FCSTD DOCUMENT  (FreeCAD 0.18RUnknown)
Label: vga_usb_serial_cutout
License: Public Domain
LicenseURL: http://en.wikipedia.org/wiki/Public_domain
objects: Sketcher::SketchObject×1, TechDraw::DrawSVGTemplate×1, TechDraw::DrawViewPart×1, TechDraw::DrawPage×1
note: 1 computed .brp shape members not serialized (recipe doc carries the construction recipe); baked Part::Feature solids carry a one-line shape summary decoded from their .brp

FEATURE [Sketcher::SketchObject] Sketch
  sketch-geometry (56):
    g0: LineSegment [constr] StartX=-35 StartY=1.6 StartZ=0 EndX=-0.6 EndY=1.6 EndZ=0
    g1: LineSegment [constr] StartX=35 StartY=1.6 StartZ=0 EndX=35 EndY=0 EndZ=0
    g2: LineSegment [constr] StartX=35 StartY=0 StartZ=0 EndX=-35 EndY=0 EndZ=0
    g3: LineSegment [constr] StartX=-35 StartY=0 StartZ=0 EndX=-35 EndY=1.6 EndZ=0
    g4: LineSegment [constr] StartX=-18.5 StartY=13.765 StartZ=0 EndX=-18.5 EndY=2.365 EndZ=0
    g5: Circle CenterX=-6 CenterY=8.065 CenterZ=0 NormalX=0 NormalY=0 NormalZ=1 AngleXU=0 Radius=1.55
    g6: Circle CenterX=-31 CenterY=8.065 CenterZ=0 NormalX=0 NormalY=0 NormalZ=1 AngleXU=0 Radius=1.55
    g7: LineSegment StartX=-25.35 StartY=13.765 StartZ=0 EndX=-11.65 EndY=13.765 EndZ=0
    g8: LineSegment StartX=-24.5389 StartY=2.365 StartZ=0 EndX=-12.4611 EndY=2.365 EndZ=0
    g9: LineSegment StartX=-28.6983 StartY=9.7746 StartZ=0 EndX=-27.8872 EndY=5.1746 EndZ=0
    g10: LineSegment StartX=-8.30165 StartY=9.7746 StartZ=0 EndX=-9.11276 EndY=5.1746 EndZ=0
    g11: ArcOfCircle CenterX=-24.5389 CenterY=5.765 CenterZ=0 NormalX=0 NormalY=0 NormalZ=1 AngleXU=0 Radius=3.4 StartAngle=3.31613 EndAngle=4.71239
    g12: ArcOfCircle CenterX=-12.4611 CenterY=5.765 CenterZ=0 NormalX=0 NormalY=0 NormalZ=1 AngleXU=0 Radius=3.4 StartAngle=4.71239 EndAngle=6.10865
    g13: ArcOfCircle CenterX=-11.65 CenterY=10.365 CenterZ=0 NormalX=0 NormalY=0 NormalZ=1 AngleXU=0 Radius=3.4 StartAngle=6.10865 EndAngle=7.85398
    g14: ArcOfCircle CenterX=-25.35 CenterY=10.365 CenterZ=0 NormalX=0 NormalY=0 NormalZ=1 AngleXU=0 Radius=3.4 StartAngle=1.5708 EndAngle=3.31613
    g15: LineSegment [constr] StartX=-28.75 StartY=13.765 StartZ=0 EndX=-28.75 EndY=2.365 EndZ=0
    g16: LineSegment [constr] StartX=-8.25 StartY=13.765 StartZ=0 EndX=-8.25 EndY=2.365 EndZ=0
    g17: GeomPoint X=-18.5 Y=8.065 Z=0
    g18: LineSegment StartX=-0.6 StartY=1.375 StartZ=0 EndX=-0.6 EndY=4.275 EndZ=0
    g19: LineSegment StartX=8.4 StartY=1.375 StartZ=0 EndX=8.4 EndY=4.275 EndZ=0
    g20: LineSegment StartX=-0.1 StartY=4.775 StartZ=0 EndX=7.9 EndY=4.775 EndZ=0
    g21: LineSegment StartX=7.9 StartY=0.875 StartZ=0 EndX=-0.1 EndY=0.875 EndZ=0
    g22: ArcOfCircle CenterX=-0.1 CenterY=4.275 CenterZ=0 NormalX=0 NormalY=0 NormalZ=1 AngleXU=0 Radius=0.5 StartAngle=1.5708 EndAngle=3.14159
    g23: ArcOfCircle CenterX=7.9 CenterY=4.275 CenterZ=0 NormalX=0 NormalY=0 NormalZ=1 AngleXU=0 Radius=0.5 StartAngle=0 EndAngle=1.5708
    g24: ArcOfCircle CenterX=7.9 CenterY=1.375 CenterZ=0 NormalX=0 NormalY=0 NormalZ=1 AngleXU=0 Radius=0.5 StartAngle=4.71239 EndAngle=6.28319
    g25: ArcOfCircle CenterX=-0.1 CenterY=1.375 CenterZ=0 NormalX=0 NormalY=0 NormalZ=1 AngleXU=0 Radius=0.5 StartAngle=3.14159 EndAngle=4.71239
    g26: LineSegment [constr] StartX=3.9 StartY=0.875 StartZ=0 EndX=3.9 EndY=1.375 EndZ=0
    g27: LineSegment [constr] StartX=8.4 StartY=1.6 StartZ=0 EndX=10.12 EndY=1.6 EndZ=0
    g28: LineSegment [constr] StartX=-0.6 StartY=2.825 StartZ=0 EndX=-0.1 EndY=2.825 EndZ=0
    g29: LineSegment [constr] StartX=0.4 StartY=4.275 StartZ=0 EndX=7.4 EndY=4.275 EndZ=0
    g30: LineSegment [constr] StartX=7.9 StartY=3.775 StartZ=0 EndX=7.9 EndY=1.875 EndZ=0
    g31: LineSegment [constr] StartX=7.4 StartY=1.375 StartZ=0 EndX=0.4 EndY=1.375 EndZ=0
    g32: LineSegment [constr] StartX=-0.1 StartY=1.875 StartZ=0 EndX=-0.1 EndY=3.775 EndZ=0
    g33: ArcOfCircle [constr] CenterX=7.4 CenterY=3.775 CenterZ=0 NormalX=0 NormalY=0 NormalZ=1 AngleXU=0 Radius=0.5 StartAngle=0 EndAngle=1.5708
    g34: ArcOfCircle [constr] CenterX=7.4 CenterY=1.875 CenterZ=0 NormalX=0 NormalY=0 NormalZ=1 AngleXU=0 Radius=0.5 StartAngle=4.71239 EndAngle=6.28319
    g35: ArcOfCircle [constr] CenterX=0.4 CenterY=1.875 CenterZ=0 NormalX=0 NormalY=0 NormalZ=1 AngleXU=0 Radius=0.5 StartAngle=3.14159 EndAngle=4.71239
    g36: ArcOfCircle [constr] CenterX=0.4 CenterY=3.775 CenterZ=0 NormalX=0 NormalY=0 NormalZ=1 AngleXU=0 Radius=0.5 StartAngle=1.5708 EndAngle=3.14159
    g37: LineSegment [constr] StartX=3.9 StartY=4.275 StartZ=0 EndX=3.9 EndY=4.775 EndZ=0
    g38: LineSegment [constr] StartX=7.9 StartY=2.825 StartZ=0 EndX=8.4 EndY=2.825 EndZ=0
    g39: LineSegment [constr] StartX=10.62 StartY=17.77 StartZ=0 EndX=25.72 EndY=17.77 EndZ=0
    g40: LineSegment [constr] StartX=25.72 StartY=17.77 StartZ=0 EndX=25.72 EndY=1.6 EndZ=0
    g41: LineSegment [constr] StartX=25.72 StartY=1.6 StartZ=0 EndX=10.62 EndY=1.6 EndZ=0
    g42: LineSegment [constr] StartX=10.62 StartY=1.6 StartZ=0 EndX=10.62 EndY=17.77 EndZ=0
    g43: LineSegment [constr] StartX=18.17 StartY=17.77 StartZ=0 EndX=18.17 EndY=1.6 EndZ=0
    g44: LineSegment StartX=10.62 StartY=18.27 StartZ=0 EndX=25.72 EndY=18.27 EndZ=0
    g45: LineSegment StartX=26.22 StartY=17.77 StartZ=0 EndX=26.22 EndY=1.6 EndZ=0
    g46: LineSegment StartX=25.72 StartY=1.1 StartZ=0 EndX=10.62 EndY=1.1 EndZ=0
    g47: LineSegment StartX=10.12 StartY=1.6 StartZ=0 EndX=10.12 EndY=17.77 EndZ=0
    g48: ArcOfCircle CenterX=10.62 CenterY=17.77 CenterZ=0 NormalX=0 NormalY=0 NormalZ=1 AngleXU=0 Radius=0.5 StartAngle=1.5708 EndAngle=3.14159
    g49: ArcOfCircle CenterX=25.72 CenterY=17.77 CenterZ=0 NormalX=0 NormalY=0 NormalZ=1 AngleXU=0 Radius=0.5 StartAngle=2.3e-15 EndAngle=1.5708
    g50: ArcOfCircle CenterX=10.62 CenterY=1.6 CenterZ=0 NormalX=0 NormalY=0 NormalZ=1 AngleXU=0 Radius=0.5 StartAngle=3.14159 EndAngle=4.71239
    g51: ArcOfCircle CenterX=25.72 CenterY=1.6 CenterZ=0 NormalX=0 NormalY=0 NormalZ=1 AngleXU=0 Radius=0.5 StartAngle=4.71239 EndAngle=6.28319
    g52: LineSegment [constr] StartX=10.62 StartY=1.6 StartZ=0 EndX=25.72 EndY=1.6 EndZ=0
    g53: LineSegment [constr] StartX=26.22 StartY=1.6 StartZ=0 EndX=35 EndY=1.6 EndZ=0
    g54: Circle CenterX=31 CenterY=7.1 CenterZ=0 NormalX=0 NormalY=0 NormalZ=1 AngleXU=0 Radius=1.8
    g55: LineSegment StartX=-35 StartY=19.27 StartZ=0 EndX=35 EndY=19.27 EndZ=0
  constraints (148):
    c: Coincident(g53,g1)
    c: Coincident(g1,g2)
    c: Coincident(g2,g3)
    c: Coincident(g3,g0)
    c: Horizontal(g2)
    c: Vertical(g1)
    c: Vertical(g3)
    c: PointOnObject(g1,g-1)
    c: Symmetric(g0,g53,g-2)
    c: DistanceY(g1,g1) = 1.6
    c: DistanceX(g2,g2) = 70
    c: Equal(g6,g5)
    c: Radius(g5) = 1.55
    c: DistanceX(g6,g5) = 25
    c: Symmetric(g6,g5,g4)
    c: Tangent(g9,g11) = -1.5708
    c: Tangent(g8,g11) = -1.5708
    c: Tangent(g8,g12) = -1.5708
    c: Tangent(g10,g12) = 1.5708
    c: Tangent(g7,g13) = 1.5708
    c: Tangent(g10,g13) = 1.5708
    c: Tangent(g9,g14) = -1.5708
    c: Tangent(g7,g14) = 1.5708
    c: Equal(g14,g11)
    c: Equal(g11,g13)
    c: Radius(g13) = 3.4
    c: Symmetric(g8,g8,g4)
    c: Symmetric(g7,g7,g4)
    c: DistanceY(g8,g7) = 11.4
    c: DistanceY(g0,g6) = 6.465
    c: Horizontal(g5,g6)
    c: PointOnObject(g4,g7)
    c: PointOnObject(g4,g8)
    c: DistanceX(g0,g6) = 4
    c: Equal(g9,g10)
    c: Vertical(g15)
    c: Tangent(g15,g14)
    c: Horizontal(g15,g7)
    c: Horizontal(g15,g8)
    c: Tangent(g16,g13)
    c: Vertical(g16)
    c: Equal(g16,g15)
    c: Horizontal(g16,g15)
    c: Angle(g15,g9) = 0.174533
    c: DistanceX(g15,g16) = 20.5
    c: Symmetric(g4,g4,g17)
    c: Horizontal(g17,g5)
    c: Vertical(g18)
    c: Vertical(g19)
    c: Horizontal(g20)
    c: Horizontal(g21)
    c: Tangent(g18,g22) = 1.5708
    c: Tangent(g20,g22) = 1.5708
    c: Tangent(g19,g23) = -1.5708
    c: Tangent(g20,g23) = 1.5708
    c: Tangent(g21,g24) = 1.5708
    c: Tangent(g19,g24) = -1.5708
    c: Tangent(g18,g25) = 1.5708
    c: Tangent(g21,g25) = 1.5708
    c: DistanceX(g18,g19) = 9
    c: Equal(g18,g19)
    c: Equal(g22,g25)
    c: Equal(g25,g24)
    c: Radius(g23) = 0.5
    c: PointOnObject(g26,g21)
    c: PointOnObject(g37,g20)
    c: Symmetric(g20,g20,g26)
    c: DistanceX(g0,g26) = 38.9
    c: Horizontal(g27)
    c: Horizontal(g0)
    c: PointOnObject(g28,g18)
    c: PointOnObject(g38,g19)
    c: Symmetric(g37,g26,g28)
    c: Horizontal(g31)
    c: Vertical(g32)
    c: Tangent(g29,g33) = 1.5708
    c: Tangent(g30,g33) = 1.5708
    c: Tangent(g31,g34) = 1.5708
    c: Tangent(g30,g34) = 1.5708
    c: Tangent(g32,g35) = 1.5708
    c: Tangent(g31,g35) = 1.5708
    c: Tangent(g32,g36) = 1.5708
    c: Tangent(g29,g36) = 1.5708
    c: Equal(g29,g31)
    c: Equal(g36,g33)
    c: Equal(g33,g34)
    c: Symmetric(g29,g29,g26)
    c: DistanceX(g32,g30) = 8
    c: DistanceY(g31,g29) = 2.9
    c: Parallel(g30,g32)
    c: DistanceY(g27,g31) = -0.225
    c: Equal(g33,g23)
    c: PointOnObject(g0,g18)
    c: PointOnObject(g26,g31)
    c: Tangent(g26,g37)
    c: PointOnObject(g37,g29)
    c: PointOnObject(g28,g32)
    c: PointOnObject(g38,g30)
    c: Tangent(g28,g38)
    c: PointOnObject(g27,g19)
    c: DistanceY(g19,g27) = 0.225
    c: DistanceY(g21,g20) = 3.9
    c: Coincident(g39,g40)
    c: Coincident(g40,g41)
    c: Coincident(g42,g39)
    c: Horizontal(g39)
    c: Horizontal(g41)
    c: Vertical(g40)
    c: Vertical(g42)
    c: DistanceX(g39,g39) = 15.1
    c: DistanceY(g40,g40) = 16.17
    c: PointOnObject(g42,g27)
    c: PointOnObject(g43,g39)
    c: PointOnObject(g43,g27)
    c: Symmetric(g39,g39,g43)
    c: DistanceX(g0,g43) = 53.17
    c: Horizontal(g44)
    c: Horizontal(g46)
    c: Vertical(g45)
    c: Vertical(g47)
    c: Tangent(g47,g48) = 1.5708
    c: Tangent(g44,g48) = 1.5708
    c: Tangent(g44,g49) = 1.5708
    c: Tangent(g45,g49) = 1.5708
    c: Tangent(g47,g50) = 1.5708
    c: Tangent(g46,g50) = 1.5708
    c: Tangent(g46,g51) = 1.5708
    c: Tangent(g45,g51) = 1.5708
    c: Equal(g51,g49)
    c: Equal(g48,g50)
    c: Radius(g49) = 0.5
    c: DistanceX(g47,g45) = 16.1
    c: Symmetric(g47,g45,g43)
    c: DistanceY(g46,g44) = 17.17
    c: PointOnObject(g27,g47)
    c: Coincident(g52,g41)
    c: Tangent(g27,g52)
    c: PointOnObject(g52,g40)
    c: PointOnObject(g53,g45)
    c: Tangent(g52,g53)
    c: Coincident(g50,g41)
    c: DistanceY(g1,g54) = 5.5
    c: DistanceX(g54,g1) = 4
    c: Radius(g54) = 1.8
    c: Horizontal(g55)
    c: Equal(g55,g2)
    c: Vertical(g55,g2)
    c: DistanceY(g44,g55) = 1
FEATURE [TechDraw::DrawSVGTemplate] Template
  EditableTexts = Approved1=SM; Approved2=SM; CheckedBy=SM; Code=Ver 1.0; CompanyName=Molten Solder Labs, 2020; DrawingNumber=License: CC0; DrawingTitle1=WD Sentinel DX4000 IO cutouts; DrawingTitle2=Serial console, 2x USB 2.0, and VGA outputs; DrawnBy=SM; Revision=^_^; Scale=Scale 1:1; Sheet=Sheet 1 of 1
  Height = 215.9
  Orientation = 1
  Width = 279.4
FEATURE [TechDraw::DrawViewPart] View
  CoarseView = false
  Direction = (0,0,1)
  Focus = 100
  HardHidden = false
  IsoCount = 0
  IsoHidden = false
  IsoVisible = false
  LockPosition = false
  Perspective = false
  Rotation = 0
  ScaleType = 0
  SeamHidden = false
  SeamVisible = false
  SmoothHidden = false
  SmoothVisible = false
  Source = -> [Sketch]
  X = 128.13
  Y = 112.862
FEATURE [TechDraw::DrawPage] Page
  KeepUpdated = true
  ProjectionType = 0
  Template = -> Template
  Views = -> [View]
